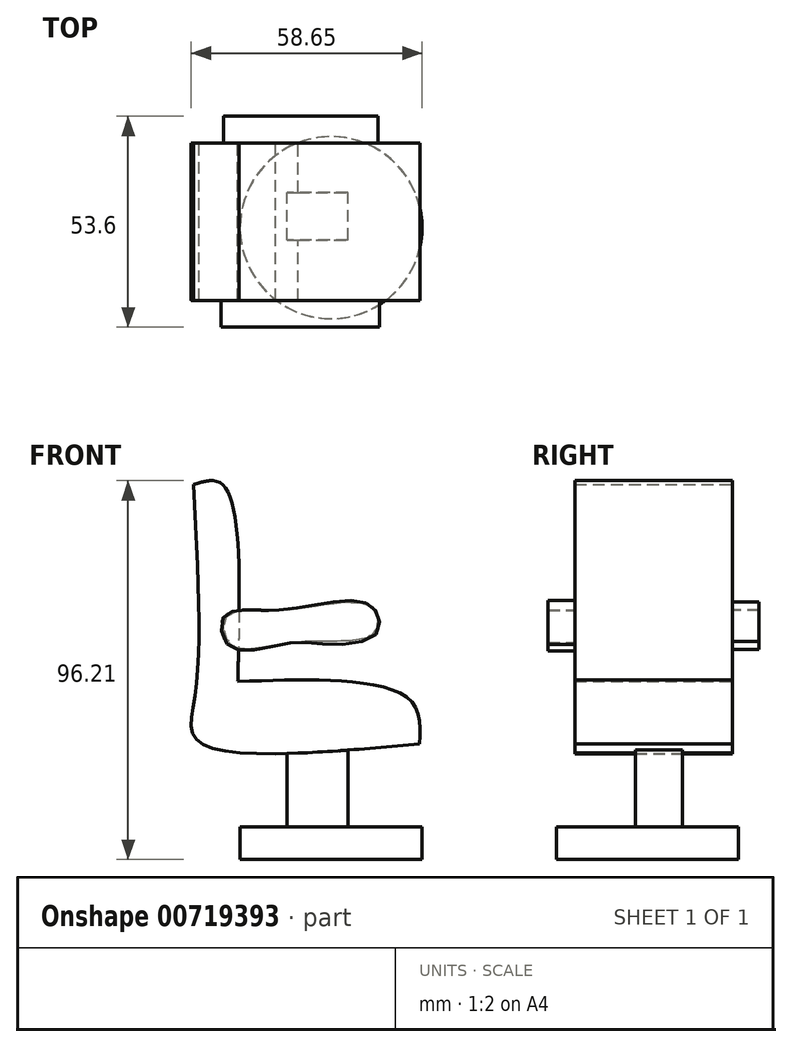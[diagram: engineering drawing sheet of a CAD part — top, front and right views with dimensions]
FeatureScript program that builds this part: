
annotation { "Feature Type Name" : "Feature", "Feature Type Description" : "" }
export const myFeature = defineFeature(function(context is Context, id is Id, definition is map)
    precondition{}
    {
        {
            var Q0;
            Q0=qCreatedBy(makeId("Front.planeOp"),FACE);
            var sketch = newSketch(context, id + "F0", { "sketchPlane" : qUnion([Q0])});
            skFitSpline(sketch, "E0", {"points": [v(-39.24, 55.28) * mm, v(-38.67, 3.15) * mm, v(-38.1, -9.83) * mm, v(18.24, -10.6) * mm], "startDerivative": vector(8.44, -151.52) * mm, "endDerivative": vector(184.24, 16.57) * mm});
            skFitSpline(sketch, "E1", {"points": [v(-39.24, 55.28) * mm, v(-31.8, 55.28) * mm, v(-27.97, 5.25) * mm], "startDerivative": vector(29.77, 9.64) * mm, "endDerivative": vector(-2.47, -94.32) * mm});
            skFitSpline(sketch, "E2", {"points": [v(-27.97, 5.25) * mm, v(0, 5.25) * mm, v(16.33, 0) * mm, v(18.24, -10.6) * mm], "startDerivative": vector(68.79, 2.74) * mm, "endDerivative": vector(-1.78, -46.1) * mm});
            skFitSpline(sketch, "E3", {"points": [v(-18.36, -13.07) * mm, v(-16.82, -39.56) * mm], "startDerivative": vector(1.54, -26.5) * mm, "endDerivative": vector(1.54, -26.5) * mm});
            skFitSpline(sketch, "E4", {"points": [v(-12.72, -12.92) * mm, v(-11.75, -39.94) * mm], "startDerivative": vector(0.97, -27.04) * mm, "endDerivative": vector(0.97, -27.04) * mm});
            skFitSpline(sketch, "E5", {"points": [v(-18.36, -13.07) * mm, v(-12.72, -12.92) * mm], "startDerivative": vector(5.64, 0.15) * mm, "endDerivative": vector(5.64, 0.15) * mm});
            skFitSpline(sketch, "E6", {"points": [v(-16.82, -39.56) * mm, v(-11.75, -39.94) * mm], "startDerivative": vector(5.07, -0.38) * mm, "endDerivative": vector(5.07, -0.38) * mm});
            skSolve(sketch);
        }
        {
            var Q0;
            Q0=qCreatedBy(makeId("Top.planeOp"),FACE);
            cPlane(context, id + "F1", {"entities" : qUnion([Q0]), "cplaneType" : CPlaneType.OFFSET, "offset" : 39.9 * mm, "oppositeDirection" : true, "width" : 150 * mm, "height" : 150 * mm});
        }
        {
            var Q0;
            {var subQ1=sQuery(id+"F0.wireOp",EDGE,"E1");Q0=makeQuery(id+"F0.imprint","IMPRINT",FACE,{"disambiguationData":[TD([[makeQuery(id+"F0.imprint","IMPRINT",EDGE,{"derivedFrom":subQ1}),-1.0]])]});}
            extrude(context, id + "F2", {"entities" : qUnion([Q0]), "depth" : 40 * mm, "offsetDistance" : 25 * mm});
        }
        {
            var Q0;
            Q0=qCreatedBy(makeId("Right.planeOp"),FACE);
            var sketch = newSketch(context, id + "F3", { "sketchPlane" : qUnion([Q0])});
            skLineSegment(sketch, "E7.bottom", {"start": v(-24.63, -9) * mm, "end": v(-12.62, -9) * mm});
            skLineSegment(sketch, "E7.top", {"start": v(-24.63, -32.39) * mm, "end": v(-12.62, -32.39) * mm});
            skLineSegment(sketch, "E7.left", {"start": v(-24.63, -9) * mm, "end": v(-24.63, -32.39) * mm});
            skLineSegment(sketch, "E7.right", {"start": v(-12.62, -9) * mm, "end": v(-12.62, -32.39) * mm});
            skSolve(sketch);
        }
        {
            var Q0;
            Q0=makeQuery(id+"F3.imprint","IMPRINT",FACE,{"disambiguationData":[TD([[makeQuery(id+"F3.imprint","IMPRINT",EDGE,{"derivedFrom":sQuery(id+"F3.wireOp",EDGE,"E7.bottom")}),-1.0]])]});
            extrude(context, id + "F4", {"entities" : qUnion([Q0]), "operationType" : NewBodyOperationType.ADD, "oppositeDirection" : true, "depth" : 15.5 * mm, "offsetDistance" : 25 * mm});
        }
        {
            var Q0;
            Q0=qCreatedBy(id+"F1.planeOp",FACE);
            var sketch = newSketch(context, id + "F5", { "sketchPlane" : qUnion([Q0])});
            skCircle(sketch, "E8", {"center": v(-4.27, -21.52) * mm, "radius": 23.13 * mm});
            skSolve(sketch);
        }
        {
            var Q0;
            Q0=makeQuery(id+"F5.imprint","IMPRINT",FACE,{"disambiguationData":[TD([[makeQuery(id+"F5.imprint","IMPRINT",EDGE,{"derivedFrom":sQuery(id+"F5.wireOp",EDGE,"E8")}),1.0]])]});
            extrude(context, id + "F6", {"entities" : qUnion([Q0]), "operationType" : NewBodyOperationType.ADD, "depth" : 8.3 * mm, "offsetDistance" : 25 * mm});
        }
        {
            var Q0;
            Q0=qCreatedBy(makeId("Front.planeOp"),FACE);
            var sketch = newSketch(context, id + "F7", { "sketchPlane" : qUnion([Q0])});
            skFitSpline(sketch, "E9", {"points": [v(-30.83, 21.8) * mm, v(-20.53, 23.35) * mm, v(-7.02, 24.65) * mm, v(6.12, 24.06) * mm, v(6.55, 17.45) * mm, v(-13.64, 15.22) * mm, v(-29.47, 14.42) * mm, v(-30.83, 21.8) * mm]});
            skSolve(sketch);
        }
        {
            var Q0;
            Q0=makeQuery(id+"F7.imprint","IMPRINT",FACE,{"disambiguationData":[TD([[makeQuery(id+"F7.imprint","IMPRINT",EDGE,{"derivedFrom":sQuery(id+"F7.wireOp",EDGE,"E9")}),-1.0]])]});
            extrude(context, id + "F8", {"entities" : qUnion([Q0]), "operationType" : NewBodyOperationType.ADD, "oppositeDirection" : true, "depth" : 6.8 * mm, "offsetDistance" : 25 * mm});
        }
        {
            var Q0;
            Q0=qCreatedBy(makeId("Front.planeOp"),FACE);
            cPlane(context, id + "F9", {"entities" : qUnion([Q0]), "cplaneType" : CPlaneType.OFFSET, "offset" : 40 * mm, "width" : 150 * mm, "height" : 150 * mm});
        }
        {
            var Q0;
            Q0=qCreatedBy(id+"F9.planeOp",FACE);
            var sketch = newSketch(context, id + "F10", { "sketchPlane" : qUnion([Q0])});
            skFitSpline(sketch, "E10", {"points": [v(-17.52, 23.42) * mm, v(-6.03, 25.14) * mm, v(4.03, 25.43) * mm, v(7.77, 21.98) * mm, v(6.62, 16.81) * mm, v(-5.17, 14.8) * mm, v(-14.65, 15.09) * mm, v(-25.86, 13.07) * mm, v(-31.32, 15.66) * mm, v(-31.6, 21.7) * mm, v(-26.72, 23.42) * mm, v(-17.52, 23.42) * mm]});
            skSolve(sketch);
        }
        {
            var Q0;
            Q0=makeQuery(id+"F10.imprint","IMPRINT",FACE,{"disambiguationData":[TD([[makeQuery(id+"F10.imprint","IMPRINT",EDGE,{"derivedFrom":sQuery(id+"F10.wireOp",EDGE,"E10")}),-1.0]])]});
            extrude(context, id + "F11", {"entities" : qUnion([Q0]), "operationType" : NewBodyOperationType.ADD, "depth" : 6.8 * mm, "offsetDistance" : 25 * mm});
        }
    });
